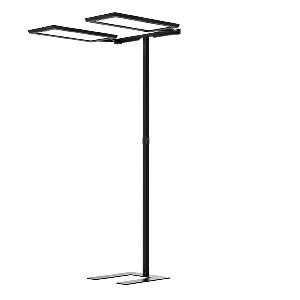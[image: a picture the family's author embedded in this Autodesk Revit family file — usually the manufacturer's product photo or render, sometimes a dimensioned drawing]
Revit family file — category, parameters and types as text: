
# Revit family: yara_doubleu_-_yus_2_15000_vtl_rx_sw_cee_s0_c_114268000-00812023_d7a3
name_source: partatom
category: Lighting Fixtures
units: mm (PartAtom-declared; Revit-internal decimal feet)

## family parameters
Cut with Voids When Loaded = No
Host = Face
Light Source = No
Part Type = Normal
Room Calculation Point = No
Round Connector Dimension = Use Diameter
Shared = No

## types (1)
- YARA.doubleU - YUS 2/15000/VTL/RX/SW/CEE/S0/C (1 x LED, 15000 lm, VTL)
    Apparent Load = 214 VA
    Approval mark = CE
    CIE Flux Codes = 58 87 97 13 100
    Color Rendering = 80-89
    Color Temperature = VTL
    Control Gear = Electronic ballast
    Default Elevation = 1800 mm
    Description = YUS 2/15000/VTL/RX/SW/CEE/S0/C|Free-standing luminaire|light source: LED Cold white   |work equipment: Electronic ballast DALI|connected load: 220-240 V, 50/60 Hz|Power consumption: approx. 210 W|power factor: approx. 0,966|luminous flux: 30000 lm|luminous efficacy: 142 lm/W|light distribution: Direct/indirect|direct ratio: approx. 13 %|color rendering index (CRI): >= 80|chromaticity tolerance:  3 SDCM|technology: Multiple daylight-dependent motion sensors|operation: Wireless switch|luminaire body|material: Aluminium/plastic|surface: Powder coatet|colour: Black|lamp cover: Acrylic (PMMA)|tubular section|material: Steel tube|surface: Powder-coated|Form: Tubular section upright|colour of tubular section: Black|luminaire base|Form: C-form flat|weight (net): approx. 26.0 kg|mains lead: 3.00 m Mains plug CEE 7/VII|Fastening: Floor standing base|glare control: Conical prismatic screen|luminance(L65): <= 2700 cd/m|unified glare rating(4H 8H): <=  16|special features: App control, Asymmetric radiation, Biodynamic light VTL, Direct and indirect lighting component with edge light and light guidetechnology for a homogeneous light exit, Flicker-free, LTX multisensor for workplace optimisation, Magnetic control panel, freely positionable, Optional LTX Cloud connection, TALK Bluetooth|Approval mark: VDE - ENEC|
    Frequency = 50 Hz, 60 Hz
    Height = 24 mm  [stored 0.0787402 ft]
    Lamp = 1 x LED
    Lamp Light Flux = 15000 lm
    Lamp count = 1
    Length = 690 mm
    Luminous efficacy = 140 lm/W
    Manufacturer = Waldmann
    ModVariant = No
    Model = 114268000-00812023
    Mounting Place = Floor
    Mounting Type = Freestanding
    Number of Poles = 1
    OnlyDefault = Yes
    Power Factor = 1
    Product Name = YARA.doubleU - YUS 2/15000/VTL/RX/SW/CEE/S0/C
    Product group = Free standing luminaire
    ProductGroupID = 13
    Protection Class = Protection class I
    Protection Degree = IP 20
    RLX_Detail_Level = 1
    RlxData = <blob elided: 71477 chars, md5=81062fa1>
    Socket = socket
    Standby Power = 0 W
    System Light Flux = 30000 lm
    System Power = 214 W
    Type Comments = Product without accessories
    Type Image = yus-rx-sw-c.jpg
    URL = http://relux.com
    VarID = ---
    Voltage = 230 V
    Voltage Range = 220-240 V
    Weight = 0.00 kg
    Width = 358 mm

note: [stored X ft] marks values corroborated as IEEE doubles in the binary element streams (Revit-internal decimal feet)

## geometry (parser evidence)
native form markers: Blend x4, Sweep x17
no freeform markers — native parametric forms only
